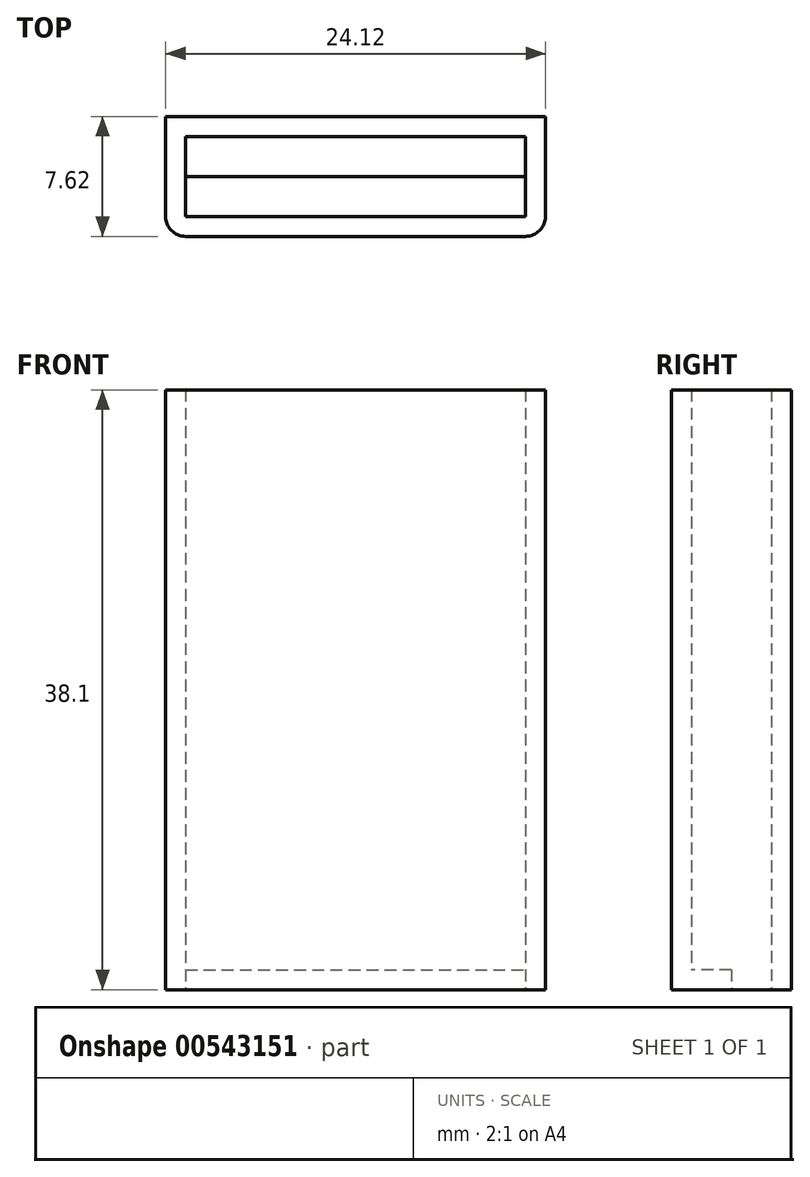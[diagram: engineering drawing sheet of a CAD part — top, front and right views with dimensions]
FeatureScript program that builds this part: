
annotation { "Feature Type Name" : "Feature", "Feature Type Description" : "" }
export const myFeature = defineFeature(function(context is Context, id is Id, definition is map)
    precondition{}
    {
        {
            var Q0;
            Q0=qCreatedBy(makeId("Top.planeOp"),FACE);
            var sketch = newSketch(context, id + "F0", { "sketchPlane" : qUnion([Q0])});
            skLineSegment(sketch, "E0.bottom", {"start": v(-12.07, 3.81) * mm, "end": v(12.07, 3.81) * mm});
            skLineSegment(sketch, "E0.top", {"start": v(-12.07, -3.8) * mm, "end": v(12.07, -3.8) * mm});
            skLineSegment(sketch, "E0.left", {"start": v(-12.07, 3.81) * mm, "end": v(-12.07, -3.81) * mm});
            skLineSegment(sketch, "E0.right", {"start": v(12.07, 3.81) * mm, "end": v(12.07, -3.81) * mm});
            skPoint(sketch, "E0.middle", {"position": v(0, 0) * mm});
            skLineSegment(sketch, "E1.bottom", {"start": v(-10.8, 2.54) * mm, "end": v(10.8, 2.54) * mm});
            skLineSegment(sketch, "E1.top", {"start": v(-10.8, -2.54) * mm, "end": v(10.8, -2.54) * mm});
            skLineSegment(sketch, "E1.left", {"start": v(-10.8, 2.54) * mm, "end": v(-10.8, -2.54) * mm});
            skLineSegment(sketch, "E1.right", {"start": v(10.8, 2.54) * mm, "end": v(10.8, -2.54) * mm});
            skSolve(sketch);
        }
        {
            var Q0;
            Q0 = qSketchRegion(id + "F0", true);
            var Q1;
            Q1=makeQuery(id+"F0.imprint","IMPRINT",FACE,{"disambiguationData":[TD([[makeQuery(id+"F0.imprint","IMPRINT",EDGE,{"derivedFrom":sQuery(id+"F0.wireOp",EDGE,"E0.bottom")}),-1.0]])]});
            extrude(context, id + "F1", {"entities" : qUnion([Q0, Q1]), "depth" : 38.1 * mm, "offsetDistance" : 25.4 * mm});
        }
        {
            var Q0;
            Q0=qCreatedBy(makeId("Top.planeOp"),FACE);
            var sketch = newSketch(context, id + "F2", { "sketchPlane" : qUnion([Q0])});
            skLineSegment(sketch, "E2.bottom", {"start": v(11.46, 0) * mm, "end": v(-11.4, 0) * mm});
            skLineSegment(sketch, "E2.top", {"start": v(11.46, -2.74) * mm, "end": v(-11.4, -2.74) * mm});
            skLineSegment(sketch, "E2.left", {"start": v(11.46, 0) * mm, "end": v(11.46, -2.74) * mm});
            skLineSegment(sketch, "E2.right", {"start": v(-11.4, 0) * mm, "end": v(-11.4, -2.74) * mm});
            skSolve(sketch);
        }
        {
            var Q0;
            Q0=makeQuery(id+"F2.imprint","IMPRINT",FACE,{"disambiguationData":[TD([[makeQuery(id+"F2.imprint","IMPRINT",EDGE,{"derivedFrom":sQuery(id+"F2.wireOp",EDGE,"E2.bottom")}),1.0]])]});
            extrude(context, id + "F3", {"entities" : qUnion([Q0]), "operationType" : NewBodyOperationType.ADD, "depth" : 1.27 * mm, "offsetDistance" : 25.4 * mm});
        }
        {
            var Q0;
            Q0=makeQuery(id+"F1.opExtrude","SWEPT_EDGE",EDGE,{"disambiguationData":[OSD([sQuery(id+"F0.wireOp",EDGE,"E0.top"),sQuery(id+"F0.wireOp",EDGE,"E0.left")])]});
            var Q1;
            Q1=makeQuery(id+"F1.opExtrude","SWEPT_EDGE",EDGE,{"disambiguationData":[OSD([sQuery(id+"F0.wireOp",EDGE,"E0.top"),sQuery(id+"F0.wireOp",EDGE,"E0.right")])]});
            fillet(context, id + "F4", {"entities" : qUnion([Q0, Q1]), "radius" : 1.27 * mm, "tangentPropagation" : true, "allowEdgeOverflow" : false});
        }
    });
